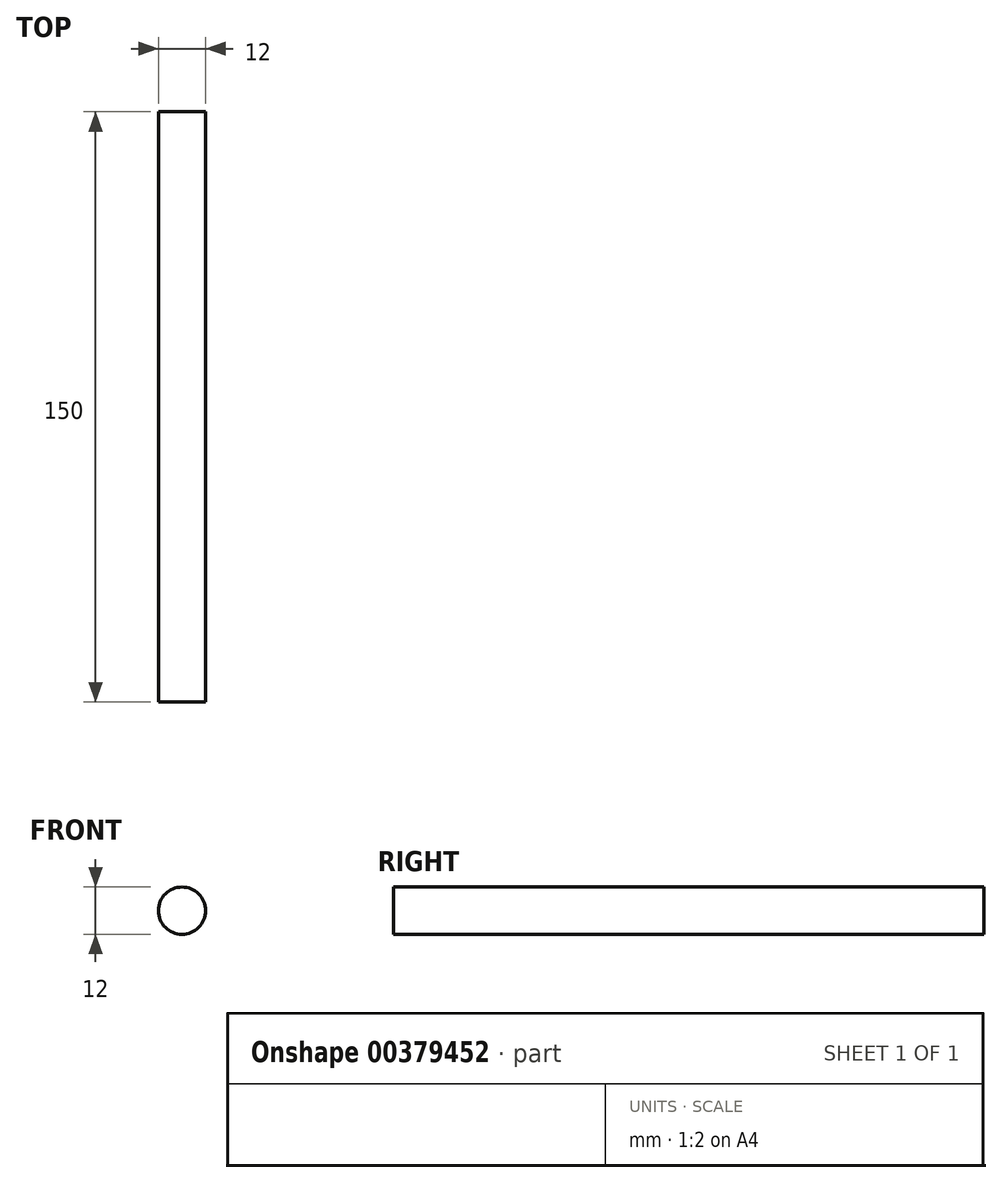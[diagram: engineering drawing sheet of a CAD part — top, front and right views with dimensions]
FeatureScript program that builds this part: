
annotation { "Feature Type Name" : "Feature", "Feature Type Description" : "" }
export const myFeature = defineFeature(function(context is Context, id is Id, definition is map)
    precondition{}
    {
        {
            var Q0;
            Q0=qCreatedBy(makeId("Front.planeOp"),FACE);
            var sketch = newSketch(context, id + "F0", { "sketchPlane" : qUnion([Q0])});
            skCircle(sketch, "E0", {"center": v(-120.18, 31.64) * mm, "radius": 6 * mm});
            skSolve(sketch);
        }
        {
            var Q0;
            Q0=makeQuery(id+"F0.imprint","IMPRINT",FACE,{"disambiguationData":[TD([[makeQuery(id+"F0.imprint","IMPRINT",EDGE,{"derivedFrom":sQuery(id+"F0.wireOp",EDGE,"E0")}),1.0]])]});
            extrude(context, id + "F1", {"entities" : qUnion([Q0]), "depth" : 150 * mm});
        }
    });
